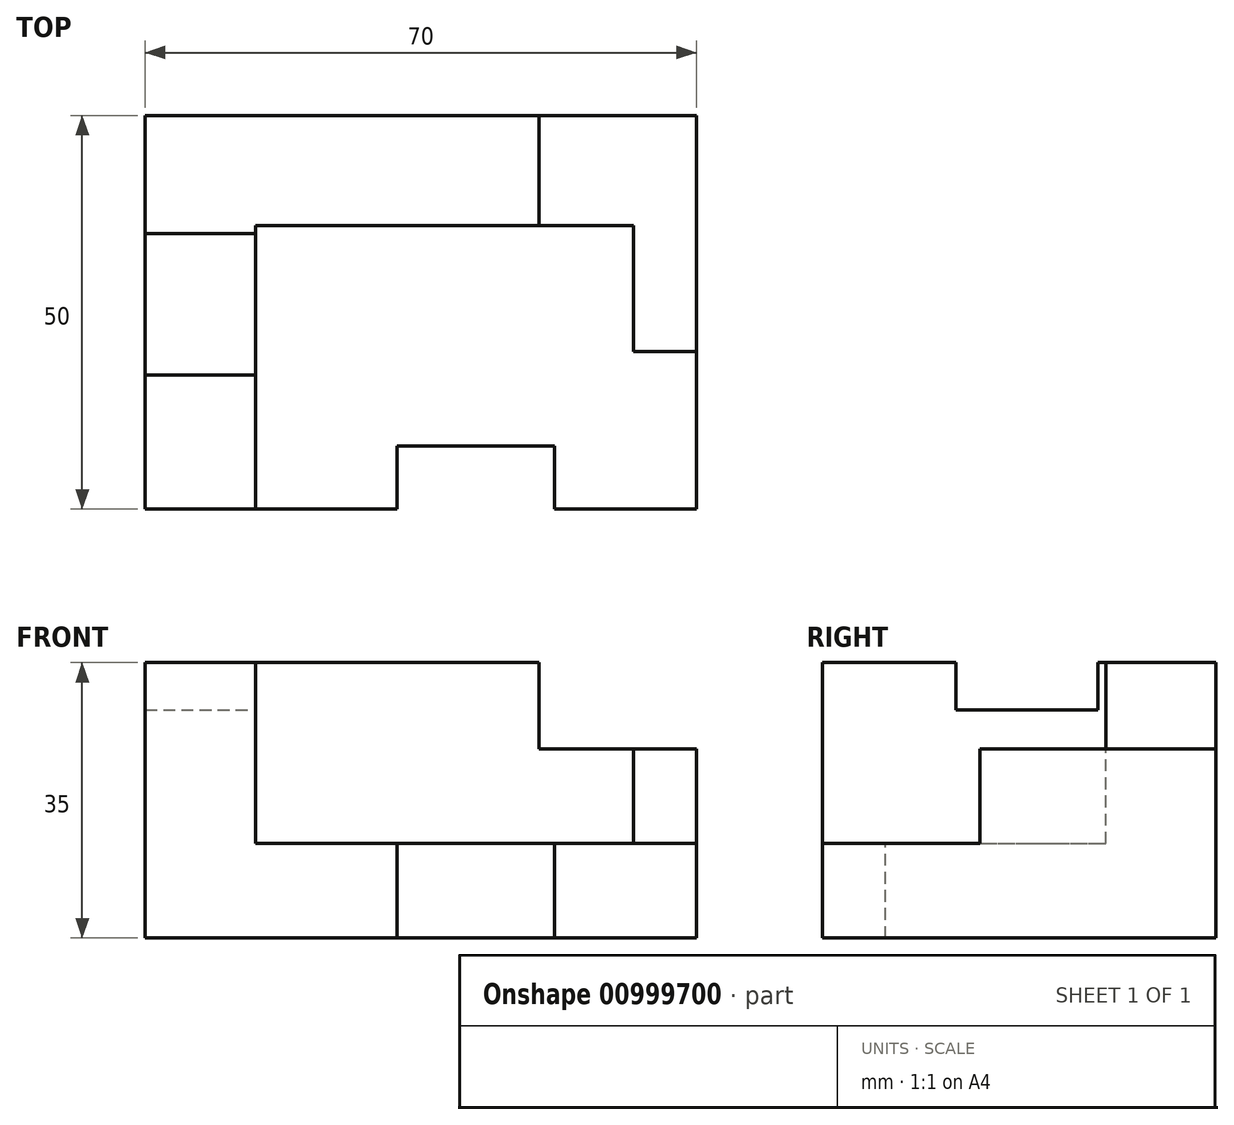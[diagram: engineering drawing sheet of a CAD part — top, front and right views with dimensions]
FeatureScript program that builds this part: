
annotation { "Feature Type Name" : "Feature", "Feature Type Description" : "" }
export const myFeature = defineFeature(function(context is Context, id is Id, definition is map)
    precondition{}
    {
        {
            var Q0;
            Q0=qCreatedBy(makeId("Front.planeOp"),FACE);
            var sketch = newSketch(context, id + "F0", { "sketchPlane" : qUnion([Q0])});
            skLineSegment(sketch, "E0", {"start": v(-33.42, 23.55) * mm, "end": v(-33.42, -11.45) * mm});
            skLineSegment(sketch, "E1", {"start": v(-33.42, -11.45) * mm, "end": v(36.58, -11.45) * mm});
            skLineSegment(sketch, "E2", {"start": v(36.58, -11.45) * mm, "end": v(36.58, 23.55) * mm});
            skLineSegment(sketch, "E3", {"start": v(36.58, 23.55) * mm, "end": v(-33.42, 23.55) * mm});
            skSolve(sketch);
        }
        {
            var Q0;
            Q0 = qSketchRegion(id + "F0", true);
            extrude(context, id + "F1", {"entities" : qUnion([Q0]), "oppositeDirection" : true, "depth" : 50 * mm, "offsetDistance" : 25 * mm});
        }
        {
            var Q0;
            Q0=makeQuery(id+"F1.opExtrude","SWEPT_FACE",FACE,{"disambiguationData":[OSD([sQuery(id+"F0.wireOp",EDGE,"E3")])]});
            var sketch = newSketch(context, id + "F2", { "sketchPlane" : qUnion([Q0])});
            skLineSegment(sketch, "E4", {"start": v(36.58, 0) * mm, "end": v(36.58, 20) * mm});
            skLineSegment(sketch, "E5", {"start": v(36.58, 20) * mm, "end": v(28.58, 20) * mm});
            skLineSegment(sketch, "E6", {"start": v(28.58, 20) * mm, "end": v(28.58, 36) * mm});
            skLineSegment(sketch, "E7", {"start": v(-33.42, 50) * mm, "end": v(16.58, 50) * mm});
            skLineSegment(sketch, "E8", {"start": v(-33.42, 50) * mm, "end": v(-33.42, 0) * mm});
            skLineSegment(sketch, "E9", {"start": v(-33.42, 0) * mm, "end": v(-19.42, 0) * mm});
            skLineSegment(sketch, "E10", {"start": v(-19.42, 0) * mm, "end": v(-19.42, 36) * mm});
            skLineSegment(sketch, "E11", {"start": v(36.58, 50) * mm, "end": v(36.58, 36) * mm});
            skLineSegment(sketch, "E12", {"start": v(36.58, 36) * mm, "end": v(36.58, 20) * mm});
            skLineSegment(sketch, "E13", {"start": v(-19.42, 36) * mm, "end": v(28.58, 36) * mm});
            skLineSegment(sketch, "E14", {"start": v(16.58, 50) * mm, "end": v(36.58, 50) * mm});
            skLineSegment(sketch, "E15", {"start": v(-19.42, 0) * mm, "end": v(36.58, 0) * mm});
            skSolve(sketch);
        }
        {
            var Q0;
            Q0=makeQuery(id+"F2.imprint","IMPRINT",FACE,{"disambiguationData":[TD([[makeQuery(id+"F2.imprint","IMPRINT",EDGE,{"derivedFrom":sQuery(id+"F2.wireOp",EDGE,"E5")}),1.0]])]});
            var Q1;
            Q1=makeQuery(id+"F2.imprint","IMPRINT",FACE,{"disambiguationData":[TD([[makeQuery(id+"F2.imprint","IMPRINT",EDGE,{"derivedFrom":sQuery(id+"F2.wireOp",EDGE,"E5")}),1.0]])]});
            extrude(context, id + "F3", {"entities" : qUnion([Q0, Q1]), "operationType" : NewBodyOperationType.REMOVE, "oppositeDirection" : true, "depth" : 23 * mm, "offsetDistance" : 25 * mm});
        }
        {
            var Q0;
            Q0=makeQuery(id+"F1.opExtrude","SWEPT_FACE",FACE,{"disambiguationData":[OSD([sQuery(id+"F0.wireOp",EDGE,"E3")])]});
            var sketch = newSketch(context, id + "F4", { "sketchPlane" : qUnion([Q0])});
            skLineSegment(sketch, "E16", {"start": v(28.58, 36) * mm, "end": v(28.58, 20) * mm});
            skLineSegment(sketch, "E17", {"start": v(28.58, 20) * mm, "end": v(36.58, 20) * mm});
            skLineSegment(sketch, "E18", {"start": v(28.58, 36) * mm, "end": v(16.58, 36) * mm});
            skLineSegment(sketch, "E19", {"start": v(16.58, 36) * mm, "end": v(16.58, 50) * mm});
            skLineSegment(sketch, "E20", {"start": v(16.58, 50) * mm, "end": v(36.58, 50) * mm});
            skLineSegment(sketch, "E21", {"start": v(36.58, 50) * mm, "end": v(36.58, 20) * mm});
            skSolve(sketch);
        }
        {
            var Q0;
            Q0=makeQuery(id+"F4.imprint","IMPRINT",FACE,{"disambiguationData":[TD([[makeQuery(id+"F4.imprint","IMPRINT",EDGE,{"derivedFrom":sQuery(id+"F4.wireOp",EDGE,"E16")}),-1.0]])]});
            extrude(context, id + "F5", {"entities" : qUnion([Q0]), "operationType" : NewBodyOperationType.REMOVE, "oppositeDirection" : true, "depth" : 11 * mm, "offsetDistance" : 25 * mm});
        }
        {
            var Q0;
            Q0=makeQuery(id+"F1.opExtrude","SWEPT_FACE",FACE,{"disambiguationData":[OSD([sQuery(id+"F0.wireOp",EDGE,"E3")])]});
            var sketch = newSketch(context, id + "F6", { "sketchPlane" : qUnion([Q0])});
            skLineSegment(sketch, "E22", {"start": v(-33.42, 50) * mm, "end": v(-33.42, 35) * mm});
            skLineSegment(sketch, "E23", {"start": v(-33.42, 35) * mm, "end": v(-19.42, 35) * mm});
            skLineSegment(sketch, "E24", {"start": v(-19.42, 35) * mm, "end": v(-19.42, 17) * mm});
            skLineSegment(sketch, "E25", {"start": v(-19.42, 17) * mm, "end": v(-33.42, 17) * mm});
            skLineSegment(sketch, "E26", {"start": v(-33.42, 17) * mm, "end": v(-33.42, 35) * mm});
            skSolve(sketch);
        }
        {
            var Q0;
            Q0=makeQuery(id+"F6.imprint","IMPRINT",FACE,{"disambiguationData":[TD([[makeQuery(id+"F6.imprint","IMPRINT",EDGE,{"derivedFrom":sQuery(id+"F6.wireOp",EDGE,"E23")}),-1.0]])]});
            extrude(context, id + "F7", {"entities" : qUnion([Q0]), "operationType" : NewBodyOperationType.REMOVE, "oppositeDirection" : true, "depth" : 6 * mm, "offsetDistance" : 25 * mm});
        }
        {
            var Q0;
            Q0=makeQuery(id+"F3.boolean.opBoolean","COPY",FACE,{"derivedFrom":makeQuery(id+"F3.opExtrude","CAP_FACE",FACE,{"disambiguationData":[OSD([sQuery(id+"F2.wireOp",EDGE,"E5"),sQuery(id+"F2.wireOp",EDGE,"E6"),sQuery(id+"F2.wireOp",EDGE,"E10"),sQuery(id+"F2.wireOp",EDGE,"E13"),sQuery(id+"F2.wireOp",EDGE,"E15"),sQuery(id+"F2.wireOp",EDGE,"E4")])],"isStart":false})});
            var sketch = newSketch(context, id + "F8", { "sketchPlane" : qUnion([Q0])});
            skLineSegment(sketch, "E27", {"start": v(-19.42, 0) * mm, "end": v(-1.42, 0) * mm});
            skLineSegment(sketch, "E28", {"start": v(-1.42, 0) * mm, "end": v(18.58, 0) * mm});
            skLineSegment(sketch, "E29", {"start": v(18.58, 0) * mm, "end": v(18.58, 8) * mm});
            skLineSegment(sketch, "E30", {"start": v(18.58, 8) * mm, "end": v(-1.42, 8) * mm});
            skLineSegment(sketch, "E31", {"start": v(-1.42, 8) * mm, "end": v(-1.42, 0) * mm});
            skSolve(sketch);
        }
        {
            var Q0;
            Q0=makeQuery(id+"F8.imprint","IMPRINT",FACE,{"disambiguationData":[TD([[makeQuery(id+"F8.imprint","IMPRINT",EDGE,{"derivedFrom":sQuery(id+"F8.wireOp",EDGE,"E28")}),-1.0]])]});
            extrude(context, id + "F9", {"entities" : qUnion([Q0]), "operationType" : NewBodyOperationType.REMOVE, "oppositeDirection" : true, "depth" : 25 * mm, "offsetDistance" : 25 * mm});
        }
    });
